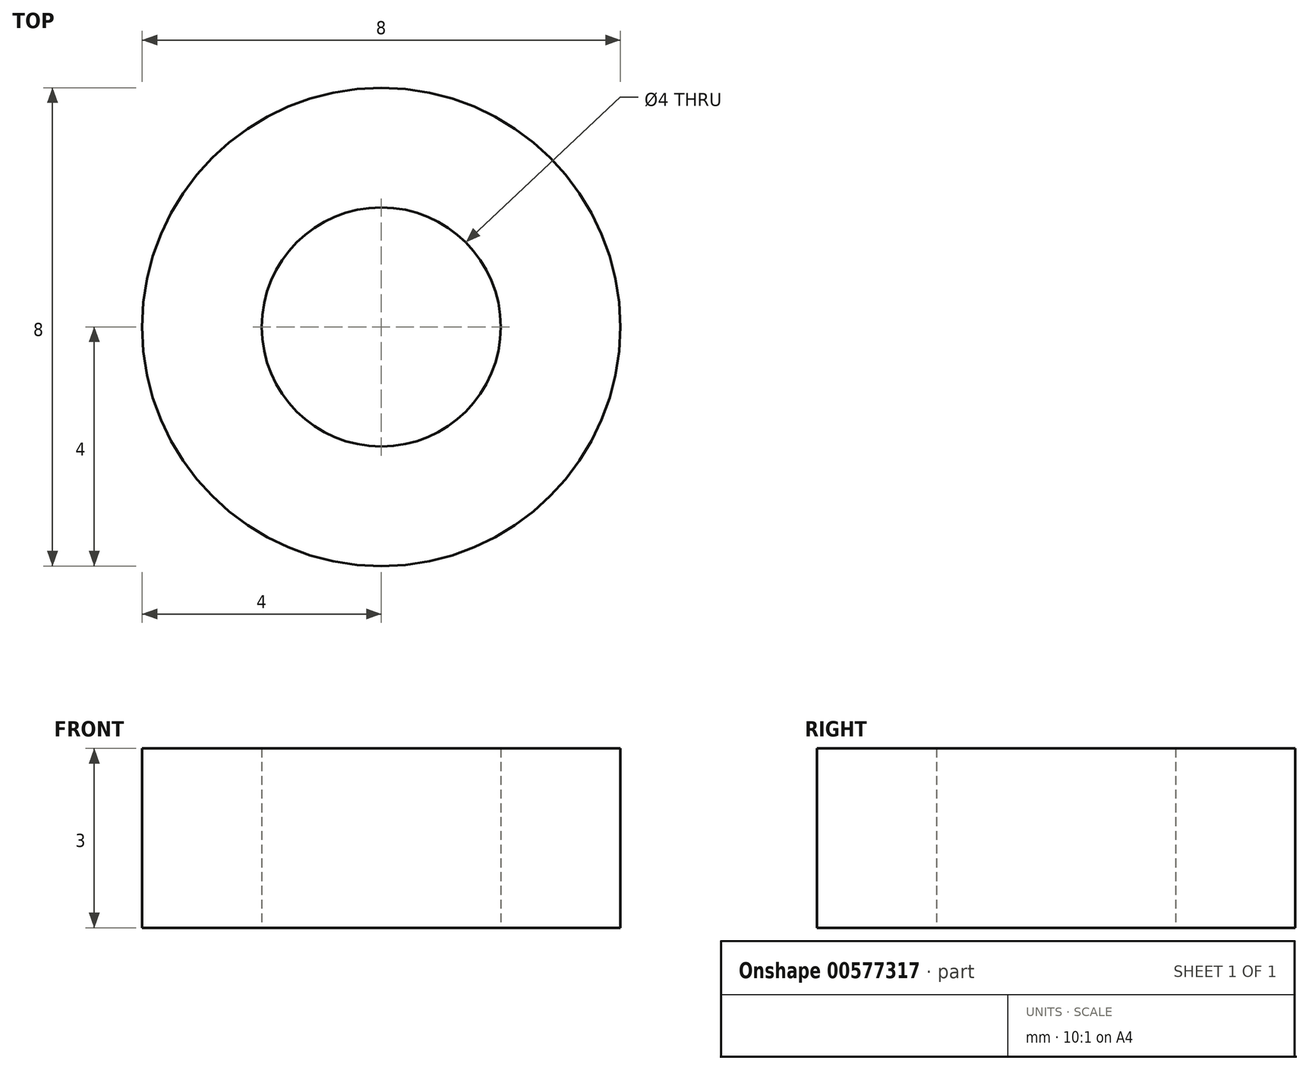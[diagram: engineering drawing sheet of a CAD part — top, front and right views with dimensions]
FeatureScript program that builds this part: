
annotation { "Feature Type Name" : "Feature", "Feature Type Description" : "" }
export const myFeature = defineFeature(function(context is Context, id is Id, definition is map)
    precondition{}
    {
        {
            var Q0;
            Q0=qCreatedBy(makeId("Top.planeOp"),FACE);
            var sketch = newSketch(context, id + "F0", { "sketchPlane" : qUnion([Q0])});
            skCircle(sketch, "E0", {"center": v(0, 0) * mm, "radius": 2 * mm});
            skCircle(sketch, "E1", {"center": v(0, 0) * mm, "radius": 4 * mm});
            skSolve(sketch);
        }
        {
            var Q0;
            Q0=makeQuery(id+"F0.imprint","IMPRINT",FACE,{"disambiguationData":[TD([[makeQuery(id+"F0.imprint","IMPRINT",EDGE,{"derivedFrom":sQuery(id+"F0.wireOp",EDGE,"E0")}),-1.0]])]});
            extrude(context, id + "F1", {"entities" : qUnion([Q0]), "depth" : 3 * mm, "offsetDistance" : 25.4 * mm});
        }
    });
